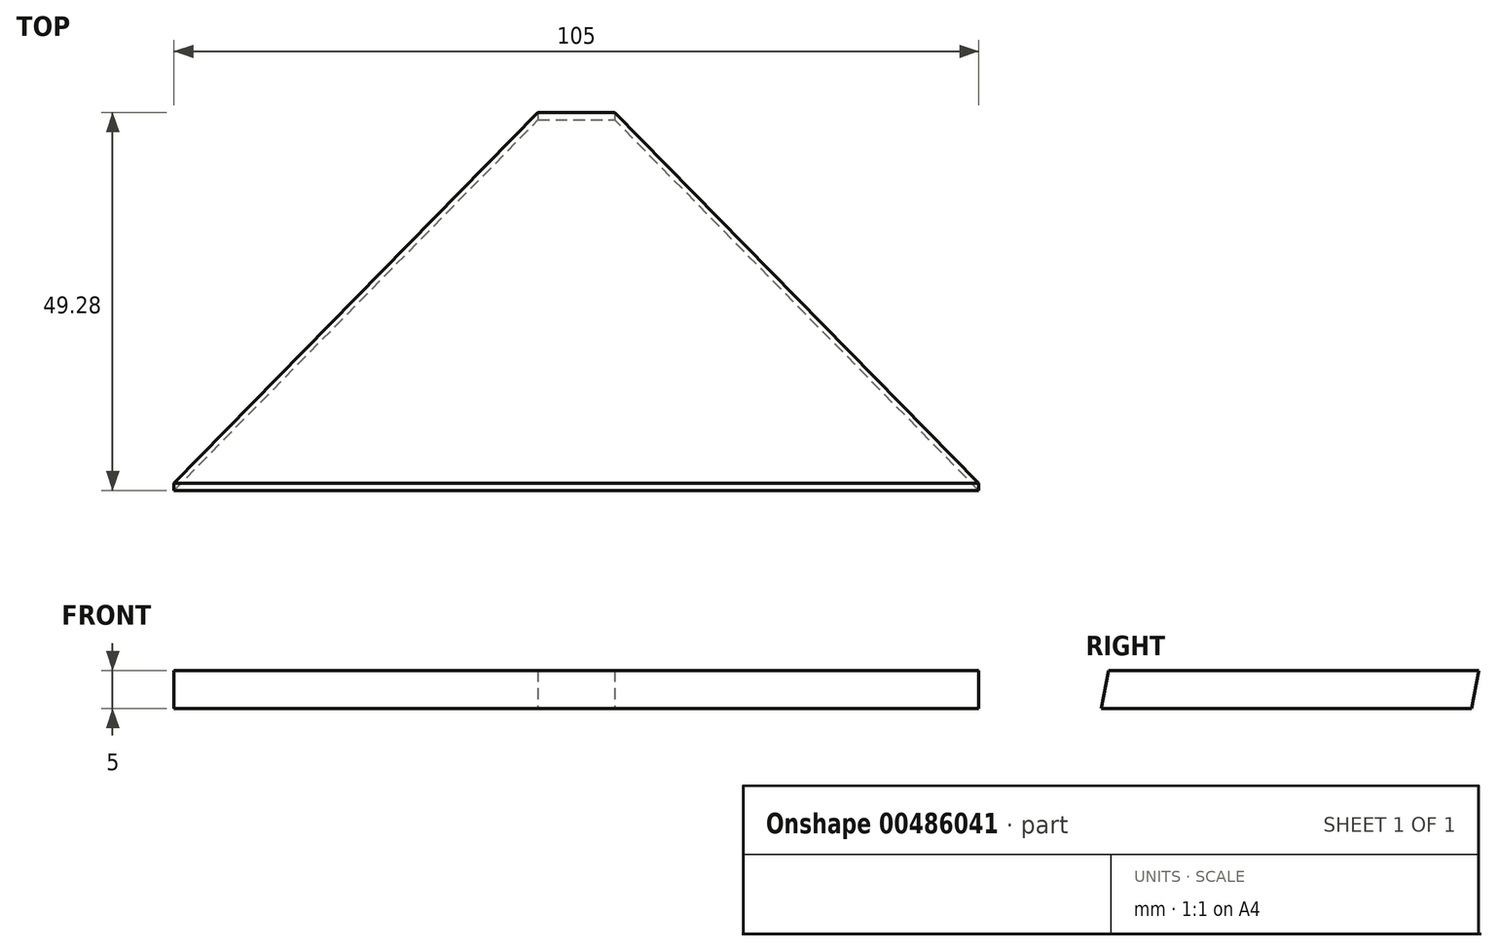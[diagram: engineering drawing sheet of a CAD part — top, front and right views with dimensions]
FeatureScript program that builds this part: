
annotation { "Feature Type Name" : "Feature", "Feature Type Description" : "" }
export const myFeature = defineFeature(function(context is Context, id is Id, definition is map)
    precondition{}
    {
        {
            var Q0;
            Q0=qCreatedBy(makeId("Top.planeOp"),FACE);
            var sketch = newSketch(context, id + "F0", { "sketchPlane" : qUnion([Q0])});
            skLineSegment(sketch, "E0.bottom", {"start": v(52.5, 26.25) * mm, "end": v(-52.5, 26.25) * mm});
            skLineSegment(sketch, "E0.top", {"start": v(52.5, -26.25) * mm, "end": v(-52.5, -26.25) * mm});
            skLineSegment(sketch, "E0.left", {"start": v(52.5, 26.25) * mm, "end": v(52.5, -26.25) * mm});
            skLineSegment(sketch, "E0.right", {"start": v(-52.5, 26.25) * mm, "end": v(-52.5, -26.25) * mm});
            skPoint(sketch, "E0.middle", {"position": v(0, 0) * mm});
            skSolve(sketch);
        }
        {
            var Q0;
            Q0=makeQuery(id+"F0.imprint","IMPRINT",FACE,{"disambiguationData":[TD([[makeQuery(id+"F0.imprint","IMPRINT",EDGE,{"derivedFrom":sQuery(id+"F0.wireOp",EDGE,"E0.bottom")}),1.0]])]});
            extrude(context, id + "F1", {"entities" : qUnion([Q0]), "depth" : 15 * mm});
        }
        {
            var Q0;
            Q0=makeQuery(id+"F1.opExtrude","SWEPT_FACE",FACE,{"disambiguationData":[OSD([sQuery(id+"F0.wireOp",EDGE,"E0.left")])]});
            var sketch = newSketch(context, id + "F2", { "sketchPlane" : qUnion([Q0])});
            skLineSegment(sketch, "E1", {"start": v(-26.25, 0) * mm, "end": v(26.25, 9.91) * mm});
            skLineSegment(sketch, "E2", {"start": v(-26.25, 5.09) * mm, "end": v(26.25, 15) * mm});
            skSolve(sketch);
        }
        {
            var Q0;
            {var subQ0=sQuery(id+"F2.wireOp",EDGE,"E2");Q0=makeQuery(id+"F2.imprint","IMPRINT",FACE,{"disambiguationData":[TD([[makeQuery(id+"F2.imprint","IMPRINT",EDGE,{"derivedFrom":subQ0}),1.0]])]});}
            var Q1;
            {var subQ0=sQuery(id+"F2.wireOp",EDGE,"E1");Q1=makeQuery(id+"F2.imprint","IMPRINT",FACE,{"disambiguationData":[TD([[makeQuery(id+"F2.imprint","IMPRINT",EDGE,{"derivedFrom":subQ0}),-1.0]])]});}
            extrude(context, id + "F3", {"entities" : qUnion([Q0, Q1]), "operationType" : NewBodyOperationType.REMOVE, "endBound" : BoundingType.THROUGH_ALL, "oppositeDirection" : true, "depth" : 25 * mm});
        }
        {
            var Q0;
            Q0=makeQuery(id+"F3.boolean.opBoolean","COPY",FACE,{"derivedFrom":makeQuery(id+"F3.opExtrude","SWEPT_FACE",FACE,{"disambiguationData":[OSD([sQuery(id+"F2.wireOp",EDGE,"E2")])]})});
            var sketch = newSketch(context, id + "F4", { "sketchPlane" : qUnion([Q0])});
            skLineSegment(sketch, "E3", {"start": v(-52.5, -24.85) * mm, "end": v(0, 28.58) * mm});
            skLineSegment(sketch, "E4", {"start": v(0, 28.58) * mm, "end": v(52.5, -24.85) * mm});
            skSolve(sketch);
        }
        {
            var Q0;
            Q0=qCreatedBy(makeId("Top.planeOp"),FACE);
            var sketch = newSketch(context, id + "F5", { "sketchPlane" : qUnion([Q0])});
            skLineSegment(sketch, "E5.0", {"start": v(-52.5, -26.25) * mm, "end": v(52.5, -26.25) * mm});
            skLineSegment(sketch, "E6.0", {"start": v(-52.5, -26.25) * mm, "end": v(-52.5, 26.25) * mm});
            skLineSegment(sketch, "E7.0", {"start": v(52.5, 26.25) * mm, "end": v(-52.5, 26.25) * mm});
            skLineSegment(sketch, "E8.0", {"start": v(52.5, -26.25) * mm, "end": v(52.5, 26.25) * mm});
            skLineSegment(sketch, "E9", {"start": v(-52.5, -26.25) * mm, "end": v(0, 26.25) * mm});
            skLineSegment(sketch, "E10.MirrorCS", {"start": v(52.5, -26.25) * mm, "end": v(0, 26.25) * mm});
            skSolve(sketch);
        }
        {
            var Q0;
            {var subQ0=sQuery(id+"F5.wireOp",EDGE,"E6.0");Q0=makeQuery(id+"F5.imprint","IMPRINT",FACE,{"disambiguationData":[TD([[makeQuery(id+"F5.imprint","IMPRINT",EDGE,{"derivedFrom":subQ0}),-1.0]])]});}
            var Q1;
            {var subQ0=sQuery(id+"F5.wireOp",EDGE,"E8.0");Q1=makeQuery(id+"F5.imprint","IMPRINT",FACE,{"disambiguationData":[TD([[makeQuery(id+"F5.imprint","IMPRINT",EDGE,{"derivedFrom":subQ0}),1.0]])]});}
            extrude(context, id + "F6", {"entities" : qUnion([Q0, Q1]), "operationType" : NewBodyOperationType.REMOVE, "endBound" : BoundingType.THROUGH_ALL, "depth" : 25 * mm});
        }
        {
            var Q0;
            Q0=qCreatedBy(makeId("Top.planeOp"),FACE);
            var sketch = newSketch(context, id + "F7", { "sketchPlane" : qUnion([Q0])});
            skLineSegment(sketch, "E11.0", {"start": v(0, 26.25) * mm, "end": v(52.5, -26.25) * mm});
            skLineSegment(sketch, "E12.0", {"start": v(-52.5, -26.25) * mm, "end": v(0, 26.25) * mm});
            skLineSegment(sketch, "E13.0.0", {"start": v(52.5, 26.25) * mm, "end": v(0, 26.25) * mm});
            skLineSegment(sketch, "E13.0.2", {"start": v(52.5, -26.25) * mm, "end": v(52.5, 26.25) * mm});
            skLineSegment(sketch, "E14.0.0", {"start": v(-52.5, 26.25) * mm, "end": v(-52.5, -26.25) * mm});
            skLineSegment(sketch, "E14.0.2", {"start": v(0, 26.25) * mm, "end": v(-52.5, 26.25) * mm});
            skLineSegment(sketch, "E15.bottom", {"start": v(-5, 26.25) * mm, "end": v(5, 26.25) * mm});
            skLineSegment(sketch, "E15.top", {"start": v(-5, 21.25) * mm, "end": v(5, 21.25) * mm});
            skLineSegment(sketch, "E15.left", {"start": v(-5, 26.25) * mm, "end": v(-5, 21.25) * mm});
            skLineSegment(sketch, "E15.right", {"start": v(5, 26.25) * mm, "end": v(5, 21.25) * mm});
            skSolve(sketch);
        }
        {
            var Q0;
            {var subQ3=sQuery(id+"F7.wireOp",EDGE,"E15.top");Q0=makeQuery(id+"F7.imprint","IMPRINT",FACE,{"disambiguationData":[TD([[makeQuery(id+"F7.imprint","IMPRINT",EDGE,{"derivedFrom":subQ3}),1.0]])]});}
            extrude(context, id + "F8", {"entities" : qUnion([Q0]), "operationType" : NewBodyOperationType.REMOVE, "endBound" : BoundingType.THROUGH_ALL, "depth" : 25 * mm});
        }
        {
            var Q0;
            Q0=makeQuery(id+"F1.opExtrude","SWEPT_BODY",BODY,{"disambiguationData":[OSD([sQuery(id+"F0.wireOp",EDGE,"E0.bottom"),sQuery(id+"F0.wireOp",EDGE,"E0.top"),sQuery(id+"F0.wireOp",EDGE,"E0.left"),sQuery(id+"F0.wireOp",EDGE,"E0.right")])]});
            var Q1;
            {var subQ0=sQuery(id+"F0.wireOp",EDGE,"E0.top");Q1=makeQuery(id+"F3.boolean.opBoolean","MERGE",EDGE,{"derivedFrom":[makeQuery(id+"F1.opExtrude","CAP_EDGE",EDGE,{"disambiguationData":[OSD([subQ0])],"isStart":true}),makeQuery(id+"F3.opExtrude","SWEPT_EDGE",EDGE,{"disambiguationData":[OSD([subQ0,sQuery(id+"F0.wireOp",EDGE,"E0.left"),sQuery(id+"F2.wireOp",EDGE,"E1")])]})]});}
            transform(context, id + "F9", {"entities" : qUnion([Q0]), "transformType" : TransformType.ROTATION, "transformAxis" : qUnion([Q1]), "angle" : 10.7 * degree, "makeCopy" : false});
        }
    });
